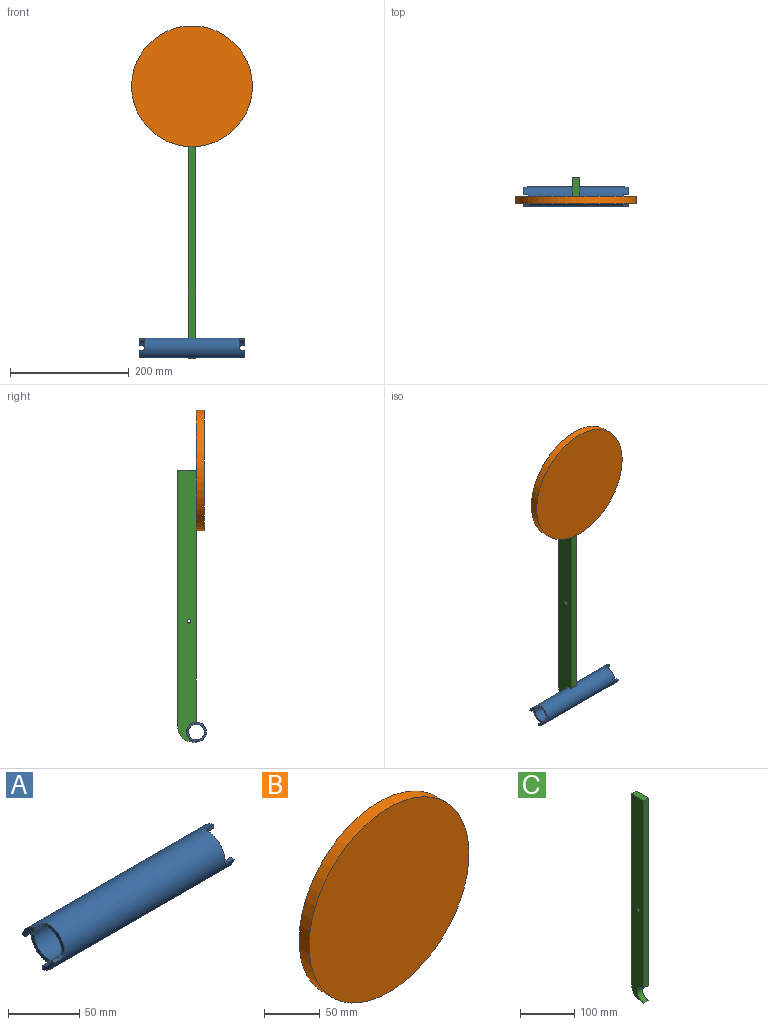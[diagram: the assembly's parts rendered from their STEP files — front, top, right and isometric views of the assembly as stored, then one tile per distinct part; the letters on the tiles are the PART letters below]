
ASSEMBLY  parts=3 mates=2
PART A: 26 faces, bbox 177.8x33.4x33.4 mm
  f0: cylinder r=13.33mm len=177.8mm, axis (-1,0,0), area 13820.4mm2, adj f2,f3,f4,f5,f6,f7,f8,f9
  f1: cylinder r=16.7mm len=177.8mm, axis (-1,0,0), area 17380.2mm2, adj f2,f3,f4,f5,f6,f7,f8,f9
  f2: plane 12.26x12.26mm, normal (-1,0,0), area 52.4mm2, adj f0,f1,f14,f17
  f3: plane 12.26x12.26mm, normal (-1,0,0), area 52.4mm2, adj f0,f1,f13,f16
  f4: plane 12.26x12.26mm, normal (1,0,0), area 52.4mm2, adj f0,f1,f8,f10
  f5: plane 12.26x12.26mm, normal (1,0,0), area 52.4mm2, adj f0,f1,f7,f11
  f6: plane 16.69x16.69mm, normal (1,0,0), area 79.3mm2, adj f0,f1,f24,f25
  f7: plane 5.56x3.49mm, normal (0,0,-1), area 19.4mm2, adj f0,f1,f5,f24
  f8: plane 5.56x3.49mm, normal (0,1,0), area 19.4mm2, adj f0,f1,f4,f25
  f9: plane 16.69x16.69mm, normal (1,0,0), area 79.3mm2, adj f0,f1,f22,f23
  f10: plane 5.56x3.49mm, normal (0,0,1), area 19.4mm2, adj f0,f1,f4,f22
  f11: plane 5.56x3.49mm, normal (0,-1,0), area 19.4mm2, adj f0,f1,f5,f23
  f12: plane 16.69x16.69mm, normal (-1,0,0), area 79.3mm2, adj f0,f1,f20,f21
  f13: plane 5.56x3.49mm, normal (0,0,1), area 19.4mm2, adj f0,f1,f3,f21
  f14: plane 5.56x3.49mm, normal (0,-1,0), area 19.4mm2, adj f0,f1,f2,f20
  f15: plane 16.69x16.69mm, normal (-1,0,0), area 79.3mm2, adj f0,f1,f18,f19
  f16: plane 5.56x3.49mm, normal (0,1,0), area 19.4mm2, adj f0,f1,f3,f18
  f17: plane 5.56x3.49mm, normal (0,0,-1), area 19.4mm2, adj f0,f1,f2,f19
  f18: cylinder r=3.97mm len=3.97mm, axis (0,0,1), area 21.4mm2, adj f0,f1,f15,f16
  f19: cylinder r=3.97mm len=3.97mm, axis (0,1,0), area 21.4mm2, adj f0,f1,f15,f17
  f20: cylinder r=3.97mm len=3.97mm, axis (0,0,-1), area 21.4mm2, adj f0,f1,f12,f14
  f21: cylinder r=3.97mm len=3.97mm, axis (0,-1,0), area 21.4mm2, adj f0,f1,f12,f13
  f22: cylinder r=3.97mm len=3.97mm, axis (0,1,0), area 21.4mm2, adj f0,f1,f9,f10
  f23: cylinder r=3.97mm len=3.97mm, axis (0,0,1), area 21.4mm2, adj f0,f1,f9,f11
  f24: cylinder r=3.97mm len=3.97mm, axis (0,-1,0), area 21.4mm2, adj f0,f1,f6,f7
  f25: cylinder r=3.97mm len=3.97mm, axis (0,0,-1), area 21.4mm2, adj f0,f1,f6,f8
PART B: 3 faces, bbox 203.2x12.7x203.2 mm
  f0: cylinder r=101.6mm len=203.2mm, axis (0,1,0), area 8107.3mm2, adj f1,f2
  f1: plane 203.2x203.2mm, normal (0,-1,0), area 32429.3mm2, adj f0
  f2: plane 203.2x203.2mm, normal (0,1,0), area 32429.3mm2, adj f0
PART C: 9 faces, bbox 12.7x31.8x457.2 mm
  f0: plane 423.8x12.7mm, normal (0,-1,0), area 5382.2mm2, adj f1,f5,f6,f7
  f1: cylinder r=16.7mm len=33.4mm, axis (-1,0,0), area 666.3mm2, adj f0,f2,f6,f7
  f2: plane 12.7x6.35mm, normal (0,0,-1), area 80.6mm2, adj f1,f3,f6,f7
  f3: cylinder r=25.4mm len=25.4mm, axis (-1,0,0), area 506.7mm2, adj f2,f4,f6,f7
  f4: plane 431.8x12.7mm, normal (0,1,0), area 5483.9mm2, adj f3,f5,f6,f7
  f5: plane 31.75x12.7mm, normal (0,0,1), area 403.2mm2, adj f0,f4,f6,f7
  f6: plane 457.2x31.75mm, normal (1,0,0), area 13907.9mm2, adj f0,f1,f2,f3,f4,f5,f8
  f7: plane 457.2x31.75mm, normal (-1,0,0), area 13907.9mm2, adj f0,f1,f2,f3,f4,f5,f8
  f8: cylinder r=3.17mm len=12.7mm, axis (1,0,0), area 253.4mm2, adj f6,f7
PLACE A t=(-101.6,0,38.1)mm fixed
PLACE B t=(-101.6,0,478.6)mm
PLACE C t=(-101.6,0,38.1)mm
MATE fastened B.f0 <-> C.f0  axis (0,1,0) through (-101.6,0,478.6)mm
MATE fastened A.f1 <-> C.f1  axis (-1,0,0) through (-101.6,0,38.1)mm
